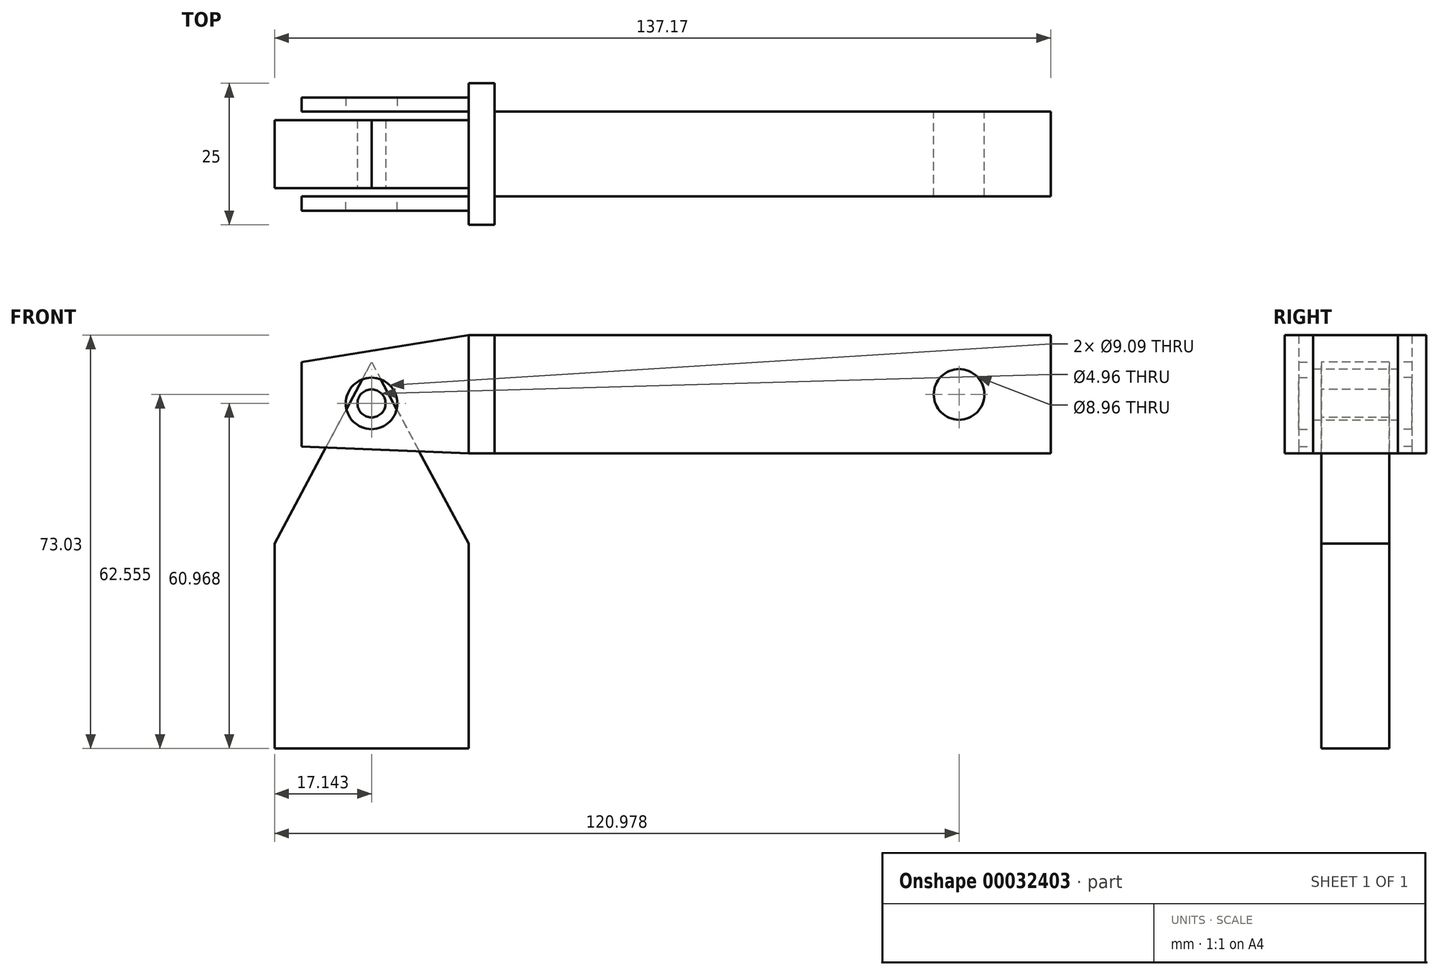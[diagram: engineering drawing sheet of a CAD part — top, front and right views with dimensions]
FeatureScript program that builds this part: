
annotation { "Feature Type Name" : "Feature", "Feature Type Description" : "" }
export const myFeature = defineFeature(function(context is Context, id is Id, definition is map)
    precondition{}
    {
        {
            var Q0;
            Q0=qCreatedBy(makeId("Front.planeOp"),FACE);
            var sketch = newSketch(context, id + "F0", { "sketchPlane" : qUnion([Q0])});
            skLineSegment(sketch, "E0.bottom", {"start": v(0, 0) * mm, "end": v(-34.3, 0) * mm});
            skLineSegment(sketch, "E0.top", {"start": v(0, 36.2) * mm, "end": v(-34.3, 36.2) * mm});
            skLineSegment(sketch, "E0.left", {"start": v(0, 0) * mm, "end": v(0, 36.2) * mm});
            skLineSegment(sketch, "E0.right", {"start": v(-34.3, 0) * mm, "end": v(-34.3, 36.2) * mm});
            skLineSegment(sketch, "E1", {"start": v(-34.3, 36.2) * mm, "end": v(-17.15, 68.27) * mm});
            skLineSegment(sketch, "E2", {"start": v(-17.15, 68.27) * mm, "end": v(0, 36.2) * mm});
            skLineSegment(sketch, "E3", {"start": v(-29.53, 53.35) * mm, "end": v(0, 52.13) * mm});
            skLineSegment(sketch, "E4", {"start": v(0, 73.03) * mm, "end": v(0, 52.13) * mm});
            skLineSegment(sketch, "E5", {"start": v(0, 52.13) * mm, "end": v(102.88, 52.13) * mm});
            skLineSegment(sketch, "E6", {"start": v(0, 73.03) * mm, "end": v(102.88, 73.03) * mm});
            skLineSegment(sketch, "E7", {"start": v(102.88, 73.03) * mm, "end": v(102.88, 52.13) * mm});
            skLineSegment(sketch, "E8.bottom", {"start": v(86.69, 73.03) * mm, "end": v(162.26, 73.03) * mm});
            skLineSegment(sketch, "E8.top", {"start": v(86.69, 52.08) * mm, "end": v(162.26, 52.08) * mm});
            skLineSegment(sketch, "E8.left", {"start": v(86.69, 73.03) * mm, "end": v(86.69, 52.08) * mm});
            skLineSegment(sketch, "E8.right", {"start": v(162.26, 73.03) * mm, "end": v(162.26, 52.08) * mm});
            skLineSegment(sketch, "E9", {"start": v(0, 73.03) * mm, "end": v(-29.53, 68.27) * mm});
            skCircle(sketch, "E10", {"center": v(-17.15, 60.97) * mm, "radius": 2.48 * mm});
            skCircle(sketch, "E11", {"center": v(-17.15, 60.97) * mm, "radius": 4.55 * mm});
            skLineSegment(sketch, "E12", {"start": v(4.57, 73.03) * mm, "end": v(4.57, 52.13) * mm});
            skLineSegment(sketch, "E13", {"start": v(-29.53, 68.27) * mm, "end": v(-29.53, 53.35) * mm});
            skLineSegment(sketch, "E14", {"start": v(107.14, 52.08) * mm, "end": v(107.14, 73.03) * mm});
            skLineSegment(sketch, "E15", {"start": v(120.7, 40.55) * mm, "end": v(91.17, 35.79) * mm});
            skLineSegment(sketch, "E16", {"start": v(91.17, 35.79) * mm, "end": v(91.17, 20.87) * mm});
            skLineSegment(sketch, "E17", {"start": v(91.17, 20.87) * mm, "end": v(120.7, 19.65) * mm});
            skLineSegment(sketch, "E18", {"start": v(120.7, 40.55) * mm, "end": v(120.7, 19.65) * mm});
            skLineSegment(sketch, "E19", {"start": v(107.14, 73.03) * mm, "end": v(80.21, 66.8) * mm});
            skLineSegment(sketch, "E20", {"start": v(80.21, 66.8) * mm, "end": v(80.21, 57.27) * mm});
            skLineSegment(sketch, "E21", {"start": v(80.21, 57.27) * mm, "end": v(107.14, 52.08) * mm});
            skCircle(sketch, "E22", {"center": v(86.69, 62.56) * mm, "radius": 4.48 * mm});
            skSolve(sketch);
        }
        {
            var Q0;
            {var subQ2=sQuery(id+"F0.wireOp",EDGE,"E4");Q0=makeQuery(id+"F0.imprint","IMPRINT",FACE,{"disambiguationData":[TD([[makeQuery(id+"F0.imprint","IMPRINT",EDGE,{"derivedFrom":subQ2}),1.0]])]});}
            extrude(context, id + "F1", {"entities" : qUnion([Q0]), "endBound" : BoundingType.SYMMETRIC, "depth" : 25 * mm});
        }
        {
            var Q0;
            {var subQ3=sQuery(id+"F0.wireOp",EDGE,"E1");var subQ5=sQuery(id+"F0.wireOp",EDGE,"E3");var subQ7=makeQuery(id+"F0.imprint","INTERSECT",VERTEX,{"derivedFrom":[subQ3,subQ5]});Q0=makeQuery(id+"F0.imprint","IMPRINT",FACE,{"disambiguationData":[TD([[makeQuery(id+"F0.imprint","IMPRINT",EDGE,{"disambiguationData":[TD([[subQ7,-1.0]])],"derivedFrom":subQ3}),-1.0]])]});}
            var Q1;
            {var subQ10=sQuery(id+"F0.wireOp",EDGE,"E4");Q1=makeQuery(id+"F0.imprint","IMPRINT",FACE,{"disambiguationData":[TD([[makeQuery(id+"F0.imprint","IMPRINT",EDGE,{"derivedFrom":subQ10}),-1.0]])]});}
            var Q2;
            {var subQ1=sQuery(id+"F0.wireOp",EDGE,"E2");var subQ3=sQuery(id+"F0.wireOp",EDGE,"E1");var subQ5=makeQuery(id+"F0.imprint","INTERSECT",VERTEX,{"derivedFrom":[subQ3,subQ1]});Q2=makeQuery(id+"F0.imprint","IMPRINT",FACE,{"disambiguationData":[TD([[makeQuery(id+"F0.imprint","IMPRINT",EDGE,{"disambiguationData":[TD([[subQ5,1.0]])],"derivedFrom":subQ3}),-1.0]])]});}
            extrude(context, id + "F2", {"entities" : qUnion([Q0, Q1, Q2]), "operationType" : NewBodyOperationType.ADD, "depth" : 10 * mm, "hasSecondDirection" : true, "secondDirectionOppositeDirection" : false, "secondDirectionDepth" : 7.5 * mm});
        }
        {
            var Q0;
            Q0=makeQuery(id+"F1.opExtrude","SWEPT_BODY",BODY,{"disambiguationData":[OSD([sQuery(id+"F0.wireOp",EDGE,"E4"),sQuery(id+"F0.wireOp",EDGE,"E5"),sQuery(id+"F0.wireOp",EDGE,"E6"),sQuery(id+"F0.wireOp",EDGE,"E12")])]});
            var Q1;
            Q1=makeQuery(id+"FxNTaal3gCcsOus_1.opPattern","COPY",BODY,{"derivedFrom":makeQuery(id+"F1.opExtrude","SWEPT_BODY",BODY,{"disambiguationData":[OSD([sQuery(id+"F0.wireOp",EDGE,"E4"),sQuery(id+"F0.wireOp",EDGE,"E5"),sQuery(id+"F0.wireOp",EDGE,"E6"),sQuery(id+"F0.wireOp",EDGE,"E12")])]}),"instanceName":"1"});
            var Q2;
            Q2=qCreatedBy(makeId("Front.planeOp"),FACE);
            mirror(context, id + "F3", {"entities" : qUnion([Q0, Q1]), "mirrorPlane" : qUnion([Q2])});
        }
        {
            var Q0;
            {var subQ0=sQuery(id+"F0.wireOp",EDGE,"E12");Q0=makeQuery(id+"F0.imprint","IMPRINT",FACE,{"disambiguationData":[TD([[makeQuery(id+"F0.imprint","IMPRINT",EDGE,{"derivedFrom":subQ0}),1.0]])]});}
            var Q1;
            {var subQ5=sQuery(id+"F0.wireOp",EDGE,"E7");Q1=makeQuery(id+"F0.imprint","IMPRINT",FACE,{"disambiguationData":[TD([[makeQuery(id+"F0.imprint","IMPRINT",EDGE,{"derivedFrom":subQ5}),-1.0]])]});}
            var Q2;
            {var subQ6=sQuery(id+"F0.wireOp",EDGE,"E7");var subQ8=sQuery(id+"F0.wireOp",EDGE,"E19");var subQ10=makeQuery(id+"F0.imprint","INTERSECT",VERTEX,{"derivedFrom":[subQ6,subQ8]});Q2=makeQuery(id+"F0.imprint","IMPRINT",FACE,{"disambiguationData":[TD([[makeQuery(id+"F0.imprint","IMPRINT",EDGE,{"disambiguationData":[TD([[subQ10,-1.0]])],"derivedFrom":subQ6}),-1.0]])]});}
            var Q3;
            {var subQ6=sQuery(id+"F0.wireOp",EDGE,"E20");Q3=makeQuery(id+"F0.imprint","IMPRINT",FACE,{"disambiguationData":[TD([[makeQuery(id+"F0.imprint","IMPRINT",EDGE,{"derivedFrom":subQ6}),1.0]])]});}
            extrude(context, id + "F4", {"entities" : qUnion([Q0, Q1, Q2, Q3]), "endBound" : BoundingType.SYMMETRIC, "depth" : 15 * mm});
        }
        {
            var Q0;
            Q0=makeQuery(id+"F0.imprint","IMPRINT",FACE,{"disambiguationData":[TD([[makeQuery(id+"F0.imprint","IMPRINT",EDGE,{"derivedFrom":sQuery(id+"F0.wireOp",EDGE,"E0.bottom")}),-1.0]])]});
            var Q1;
            {var subQ5=sQuery(id+"F0.wireOp",EDGE,"E0.top");Q1=makeQuery(id+"F0.imprint","IMPRINT",FACE,{"disambiguationData":[TD([[makeQuery(id+"F0.imprint","IMPRINT",EDGE,{"derivedFrom":subQ5}),-1.0]])]});}
            var Q2;
            {var subQ3=sQuery(id+"F0.wireOp",EDGE,"E1");var subQ5=sQuery(id+"F0.wireOp",EDGE,"E3");var subQ7=makeQuery(id+"F0.imprint","INTERSECT",VERTEX,{"derivedFrom":[subQ3,subQ5]});Q2=makeQuery(id+"F0.imprint","IMPRINT",FACE,{"disambiguationData":[TD([[makeQuery(id+"F0.imprint","IMPRINT",EDGE,{"disambiguationData":[TD([[subQ7,-1.0]])],"derivedFrom":subQ3}),-1.0]])]});}
            var Q3;
            Q3=makeQuery(id+"F0.imprint","IMPRINT",FACE,{"disambiguationData":[TD([[makeQuery(id+"F0.imprint","IMPRINT",EDGE,{"derivedFrom":sQuery(id+"F0.wireOp",EDGE,"E10")}),-1.0]])]});
            var Q4;
            {var subQ1=sQuery(id+"F0.wireOp",EDGE,"E2");var subQ3=sQuery(id+"F0.wireOp",EDGE,"E1");var subQ5=makeQuery(id+"F0.imprint","INTERSECT",VERTEX,{"derivedFrom":[subQ3,subQ1]});Q4=makeQuery(id+"F0.imprint","IMPRINT",FACE,{"disambiguationData":[TD([[makeQuery(id+"F0.imprint","IMPRINT",EDGE,{"disambiguationData":[TD([[subQ5,1.0]])],"derivedFrom":subQ3}),-1.0]])]});}
            var Q5;
            Q5=makeQuery(id+"F3.opPattern","COPY",FACE,{"derivedFrom":makeQuery(id+"F2.opExtrude","CAP_FACE",FACE,{"disambiguationData":[OSD([sQuery(id+"F0.wireOp",EDGE,"E1"),sQuery(id+"F0.wireOp",EDGE,"E2"),sQuery(id+"F0.wireOp",EDGE,"E3"),sQuery(id+"F0.wireOp",EDGE,"E4"),sQuery(id+"F0.wireOp",EDGE,"E9"),sQuery(id+"F0.wireOp",EDGE,"E11"),sQuery(id+"F0.wireOp",EDGE,"E13")])],"isStart":true}),"instanceName":"1"});
            extrude(context, id + "F5", {"entities" : qUnion([Q0, Q1, Q2, Q3, Q4]), "endBound" : BoundingType.SYMMETRIC, "oppositeDirection" : true, "endBoundEntityFace" : qUnion([Q5]), "depth" : 12 * mm});
        }
    });
